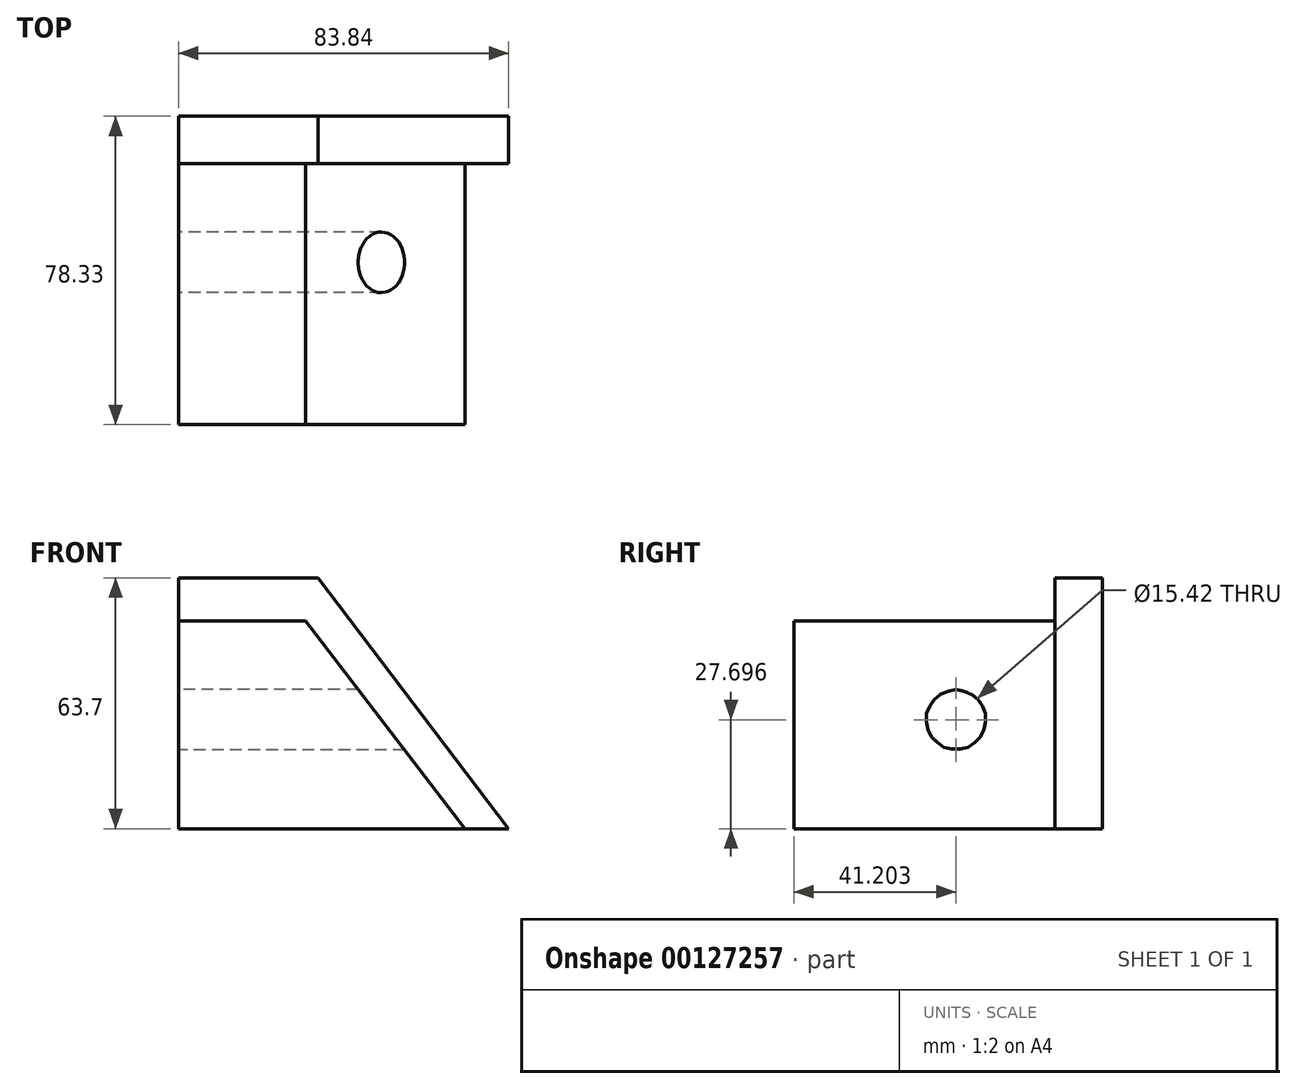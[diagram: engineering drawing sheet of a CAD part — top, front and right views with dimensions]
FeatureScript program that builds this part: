
annotation { "Feature Type Name" : "Feature", "Feature Type Description" : "" }
export const myFeature = defineFeature(function(context is Context, id is Id, definition is map)
    precondition{}
    {
        {
            var Q0;
            Q0=qCreatedBy(makeId("Front.planeOp"),FACE);
            var sketch = newSketch(context, id + "F0", { "sketchPlane" : qUnion([Q0])});
            skLineSegment(sketch, "E0", {"start": v(0, 0) * mm, "end": v(-72.8, 0) * mm});
            skLineSegment(sketch, "E1", {"start": v(-72.8, 0) * mm, "end": v(-72.8, 52.8) * mm});
            skLineSegment(sketch, "E2", {"start": v(-72.8, 52.8) * mm, "end": v(-40.57, 52.8) * mm});
            skLineSegment(sketch, "E3", {"start": v(-40.57, 52.8) * mm, "end": v(0, 0) * mm});
            skSolve(sketch);
        }
        {
            var Q0;
            Q0=makeQuery(id+"F0.imprint","IMPRINT",FACE,{"disambiguationData":[TD([[makeQuery(id+"F0.imprint","IMPRINT",EDGE,{"derivedFrom":sQuery(id+"F0.wireOp",EDGE,"E0")}),-1.0]])]});
            extrude(context, id + "F1", {"entities" : qUnion([Q0]), "depth" : 78.33 * mm});
        }
        {
            var Q0;
            Q0=makeQuery(id+"F1.opExtrude","SWEPT_FACE",FACE,{"disambiguationData":[OSD([sQuery(id+"F0.wireOp",EDGE,"E1")])]});
            var sketch = newSketch(context, id + "F2", { "sketchPlane" : qUnion([Q0])});
            skCircle(sketch, "E4", {"center": v(37.13, 27.7) * mm, "radius": 7.7 * mm});
            skSolve(sketch);
        }
        {
            var Q0;
            Q0=makeQuery(id+"F2.imprint","IMPRINT",FACE,{"disambiguationData":[TD([[makeQuery(id+"F2.imprint","IMPRINT",EDGE,{"derivedFrom":sQuery(id+"F2.wireOp",EDGE,"E4")}),1.0]])]});
            extrude(context, id + "F3", {"entities" : qUnion([Q0]), "operationType" : NewBodyOperationType.REMOVE, "oppositeDirection" : true, "depth" : 69 * mm});
        }
        {
            var Q0;
            Q0=makeQuery(id+"F1.opExtrude","CAP_FACE",FACE,{"disambiguationData":[OSD([sQuery(id+"F0.wireOp",EDGE,"E0"),sQuery(id+"F0.wireOp",EDGE,"E1"),sQuery(id+"F0.wireOp",EDGE,"E2"),sQuery(id+"F0.wireOp",EDGE,"E3")])],"isStart":true});
            var sketch = newSketch(context, id + "F4", { "sketchPlane" : qUnion([Q0])});
            skLineSegment(sketch, "E5", {"start": v(40.57, 52.8) * mm, "end": v(72.8, 52.8) * mm});
            skLineSegment(sketch, "E6", {"start": v(72.8, 52.8) * mm, "end": v(72.8, 63.7) * mm});
            skLineSegment(sketch, "E7", {"start": v(72.8, 63.7) * mm, "end": v(37.42, 63.7) * mm});
            skLineSegment(sketch, "E8", {"start": v(37.42, 63.7) * mm, "end": v(-11.03, 0) * mm});
            skLineSegment(sketch, "E9", {"start": v(-11.03, 0) * mm, "end": v(0, 0) * mm});
            skLineSegment(sketch, "E10", {"start": v(0, 0) * mm, "end": v(40.57, 52.8) * mm});
            skSolve(sketch);
        }
        {
            var Q0;
            Q0=makeQuery(id+"F4.imprint","IMPRINT",FACE,{"disambiguationData":[TD([[makeQuery(id+"F4.imprint","IMPRINT",EDGE,{"derivedFrom":sQuery(id+"F4.wireOp",EDGE,"E5")}),-1.0]])]});
            extrude(context, id + "F5", {"entities" : qUnion([Q0]), "operationType" : NewBodyOperationType.ADD, "oppositeDirection" : true, "depth" : 12 * mm});
        }
    });
